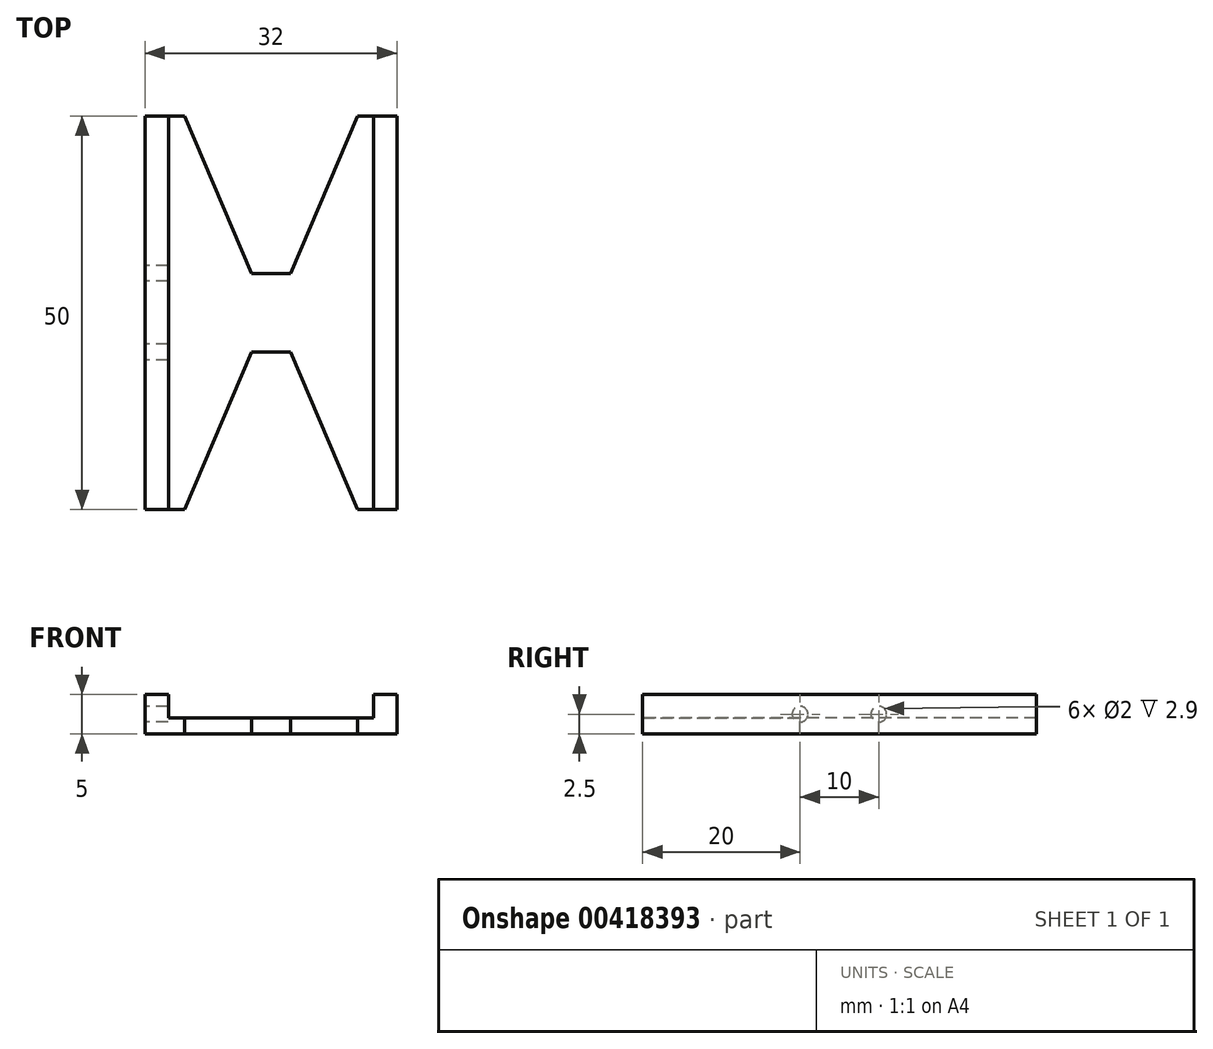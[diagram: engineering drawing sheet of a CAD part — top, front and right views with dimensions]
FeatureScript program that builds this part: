
annotation { "Feature Type Name" : "Feature", "Feature Type Description" : "" }
export const myFeature = defineFeature(function(context is Context, id is Id, definition is map)
    precondition{}
    {
        {
            var Q0;
            Q0=qCreatedBy(makeId("Top.planeOp"),FACE);
            var sketch = newSketch(context, id + "F0", { "sketchPlane" : qUnion([Q0])});
            skLineSegment(sketch, "E0.bottom", {"start": v(16, 25) * mm, "end": v(-16, 25) * mm});
            skLineSegment(sketch, "E0.top", {"start": v(16, -25) * mm, "end": v(-16, -25) * mm});
            skLineSegment(sketch, "E0.left", {"start": v(16, 25) * mm, "end": v(16, -25) * mm});
            skLineSegment(sketch, "E0.right", {"start": v(-16, 25) * mm, "end": v(-16, -25) * mm});
            skPoint(sketch, "E0.middle", {"position": v(0, 0) * mm});
            skSolve(sketch);
        }
        {
            var Q0;
            Q0 = qSketchRegion(id + "F0", true);
            extrude(context, id + "F1", {"entities" : qUnion([Q0]), "depth" : 5 * mm});
        }
        {
            var Q0;
            Q0=makeQuery(id+"F1.opExtrude","CAP_FACE",FACE,{"disambiguationData":[OSD([sQuery(id+"F0.wireOp",EDGE,"E0.bottom"),sQuery(id+"F0.wireOp",EDGE,"E0.top"),sQuery(id+"F0.wireOp",EDGE,"E0.left"),sQuery(id+"F0.wireOp",EDGE,"E0.right")])],"isStart":false});
            var sketch = newSketch(context, id + "F2", { "sketchPlane" : qUnion([Q0])});
            skLineSegment(sketch, "E1", {"start": v(-11, 25) * mm, "end": v(-2.5, 5) * mm});
            skLineSegment(sketch, "E2", {"start": v(-2.5, 5) * mm, "end": v(0, 5) * mm});
            skLineSegment(sketch, "E3.MirrorCS", {"start": v(11, 25) * mm, "end": v(2.5, 5) * mm});
            skLineSegment(sketch, "E4.MirrorCS", {"start": v(2.5, 5) * mm, "end": v(0, 5) * mm});
            skLineSegment(sketch, "E5.MirrorCS", {"start": v(-2.5, -5) * mm, "end": v(0, -5) * mm});
            skLineSegment(sketch, "E6.MirrorCS", {"start": v(2.5, -5) * mm, "end": v(0, -5) * mm});
            skLineSegment(sketch, "E7.MirrorCS", {"start": v(-11, -25) * mm, "end": v(-2.5, -5) * mm});
            skLineSegment(sketch, "E8.MirrorCS", {"start": v(11, -25) * mm, "end": v(2.5, -5) * mm});
            skLineSegment(sketch, "E9", {"start": v(-11, 25) * mm, "end": v(11, 25) * mm});
            skLineSegment(sketch, "E10", {"start": v(-11, -25) * mm, "end": v(11, -25) * mm});
            skSolve(sketch);
        }
        {
            var Q0;
            Q0 = qSketchRegion(id + "F2", true);
            extrude(context, id + "F3", {"entities" : qUnion([Q0]), "operationType" : NewBodyOperationType.REMOVE, "endBound" : BoundingType.UP_TO_NEXT, "oppositeDirection" : true, "depth" : 25 * mm});
        }
        {
            var Q0;
            Q0=makeQuery(id+"F1.opExtrude","SWEPT_FACE",FACE,{"disambiguationData":[OSD([sQuery(id+"F0.wireOp",EDGE,"E0.right")])]});
            var sketch = newSketch(context, id + "F4", { "sketchPlane" : qUnion([Q0])});
            skCircle(sketch, "E11", {"center": v(-5, 2.5) * mm, "radius": 1 * mm});
            skPoint(sketch, "E11.centerSnap0", {"position": v(-25, 2.5) * mm});
            skCircle(sketch, "E12", {"center": v(5, 2.5) * mm, "radius": 1 * mm});
            skSolve(sketch);
        }
        {
            var Q0;
            Q0 = qSketchRegion(id + "F4", true);
            extrude(context, id + "F5", {"entities" : qUnion([Q0]), "operationType" : NewBodyOperationType.REMOVE, "oppositeDirection" : true, "depth" : 2.9 * mm});
        }
        {
            var Q0;
            Q0=makeQuery(id+"F1.opExtrude","CAP_FACE",FACE,{"disambiguationData":[OSD([sQuery(id+"F0.wireOp",EDGE,"E0.bottom"),sQuery(id+"F0.wireOp",EDGE,"E0.top"),sQuery(id+"F0.wireOp",EDGE,"E0.left"),sQuery(id+"F0.wireOp",EDGE,"E0.right")])],"isStart":false});
            var sketch = newSketch(context, id + "F6", { "sketchPlane" : qUnion([Q0])});
            skLineSegment(sketch, "E13", {"start": v(-13, 25) * mm, "end": v(-13, -25) * mm});
            skPoint(sketch, "E13.endSnap0", {"position": v(-13.5, -25) * mm});
            skLineSegment(sketch, "E14", {"start": v(-13, 25) * mm, "end": v(-11, 25) * mm});
            skLineSegment(sketch, "E15.0", {"start": v(-11, 25) * mm, "end": v(-2.5, 5) * mm});
            skLineSegment(sketch, "E16.0", {"start": v(-2.5, 5) * mm, "end": v(2.5, 5) * mm});
            skLineSegment(sketch, "E17.MirrorCS", {"start": v(13, 25) * mm, "end": v(11, 25) * mm});
            skLineSegment(sketch, "E18.MirrorCS", {"start": v(11, 25) * mm, "end": v(2.5, 5) * mm});
            skLineSegment(sketch, "E19.MirrorCS", {"start": v(2.5, 5) * mm, "end": v(-2.5, 5) * mm});
            skLineSegment(sketch, "E20.MirrorCS", {"start": v(13, 25) * mm, "end": v(13, -25) * mm});
            skLineSegment(sketch, "E21.MirrorCS", {"start": v(13, -25) * mm, "end": v(11, -25) * mm});
            skLineSegment(sketch, "E22.MirrorCS", {"start": v(-13, -25) * mm, "end": v(-11, -25) * mm});
            skLineSegment(sketch, "E23.MirrorCS", {"start": v(-2.5, -5) * mm, "end": v(2.5, -5) * mm});
            skLineSegment(sketch, "E24.MirrorCS", {"start": v(2.5, -5) * mm, "end": v(-2.5, -5) * mm});
            skLineSegment(sketch, "E25.MirrorCS", {"start": v(11, -25) * mm, "end": v(2.5, -5) * mm});
            skLineSegment(sketch, "E26.MirrorCS", {"start": v(-11, -25) * mm, "end": v(-2.5, -5) * mm});
            skSolve(sketch);
        }
        {
            var Q0;
            Q0 = qSketchRegion(id + "F6", true);
            extrude(context, id + "F7", {"entities" : qUnion([Q0]), "operationType" : NewBodyOperationType.REMOVE, "oppositeDirection" : true, "depth" : 3 * mm});
        }
    });
